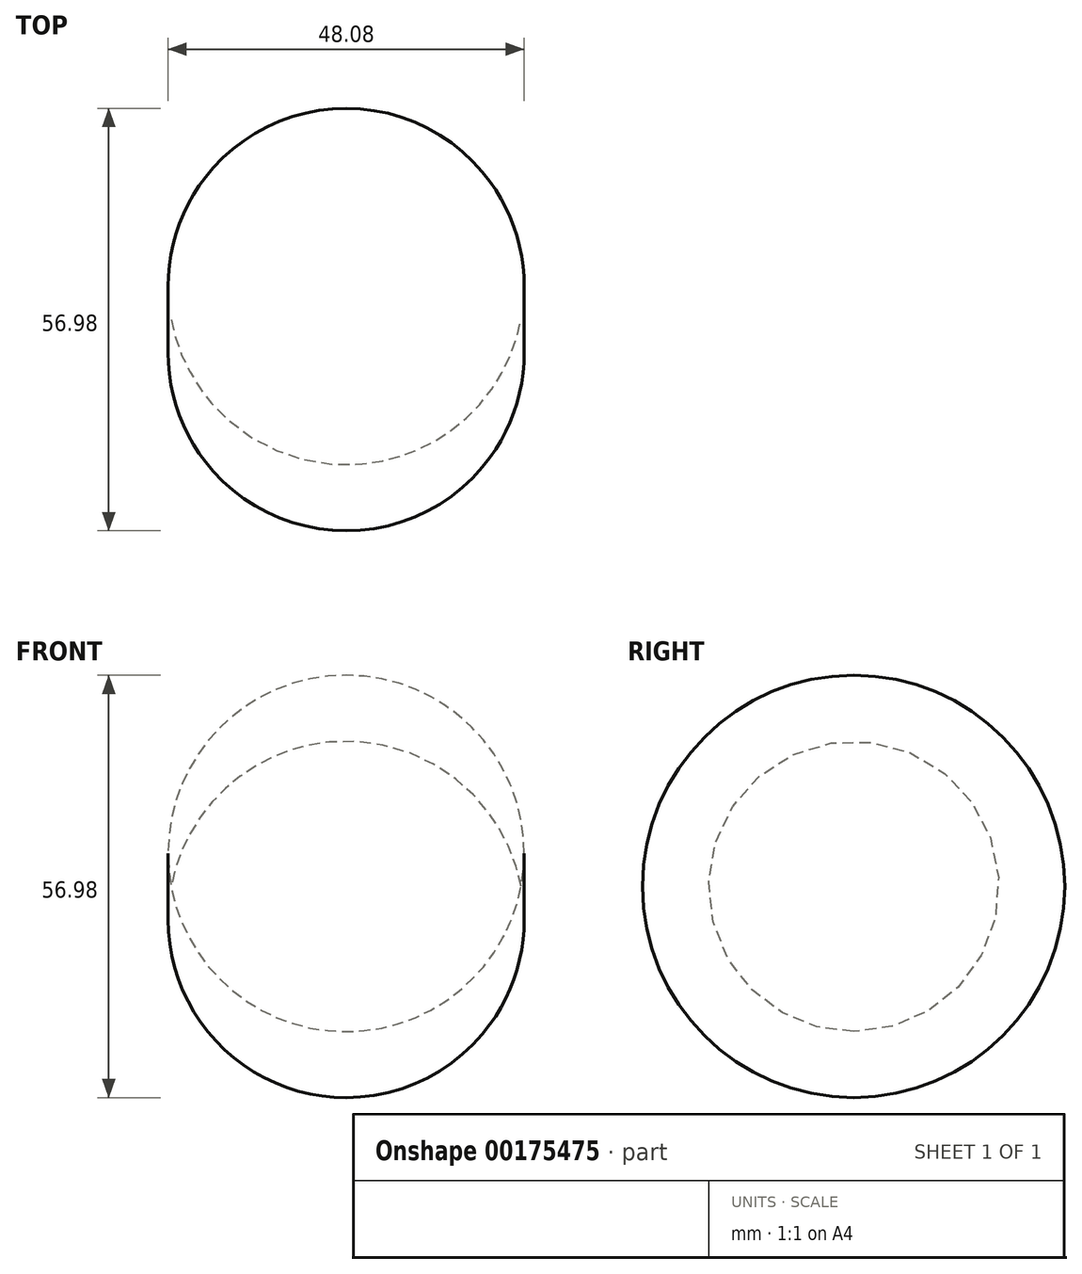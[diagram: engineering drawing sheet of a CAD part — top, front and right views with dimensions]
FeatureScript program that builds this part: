
annotation { "Feature Type Name" : "Feature", "Feature Type Description" : "" }
export const myFeature = defineFeature(function(context is Context, id is Id, definition is map)
    precondition{}
    {
        {
            var Q0;
            Q0=qCreatedBy(makeId("Front.planeOp"),FACE);
            var sketch = newSketch(context, id + "F0", { "sketchPlane" : qUnion([Q0])});
            skPoint(sketch, "E0.start.orphan", {"position": v(-24.15, 0) * mm});
            skLineSegment(sketch, "E1", {"start": v(-12.84, 0) * mm, "end": v(10.27, 0) * mm});
            skLineSegment(sketch, "E2", {"start": v(-24.15, 0) * mm, "end": v(23.1, 0) * mm});
            skArc(sketch, "E3", {"start": v(-24.15, 0) * mm, "mid": v(-0.53, -19.58) * mm, "end": v(23.1, 0) * mm});
            skSolve(sketch);
        }
        {
            var Q0;
            {var subQ0=sQuery(id+"F0.wireOp",EDGE,"E3");Q0=makeQuery(id+"F0.imprint","IMPRINT",FACE,{"disambiguationData":[TD([[makeQuery(id+"F0.imprint","IMPRINT",EDGE,{"derivedFrom":subQ0}),1.0]])]});}
            var Q1;
            Q1=sQuery(id+"F0.wireOp",EDGE,"E2");
            revolve(context, id + "F1", {"entities" : qUnion([Q0]), "axis" : qUnion([Q1]), "revolveType" : RevolveType.FULL});
        }
    });
